# Revit family: Catena UL LED - Folded
name_source: partatom
category: Lighting Fixtures
units: mm (PartAtom-declared; Revit-internal decimal feet)

## family parameters
Always vertical = Yes
Cut with Voids When Loaded = No
Host = Wall
Light Source = Yes
OmniClass Number = 23.80.70.00
OmniClass Title = Lighting
Part Type = Normal
Room Calculation Point = No
Round Connector Dimension = Use Diameter
Shared = No

## types (2) — shared parameters
Color Filter = 16777215
Dimmable = No
Dimming Lamp Color Temperature Shift = <None>
Driver Included = Yes
Driver Required = No
Emit from Line Length = 610 mm
Main Finish = Polished Chrome
Manufacturer = Astro Lighting Ltd
Product Name = Catena LED
URL = www.astrolighting.com
zero-valued in all types: Default Elevation

## per-type parameters (varying)
| type | ADA compliant | Apparent Load | Dimming Method | Efficacy (lm/w) | Electrical Class | Lamp | Length of Cable Supplied | Light Source Fixed | Location rating | Main Material | Photometric Web File | Power (Watts) | Product Code | Product Location | Product SKU | Tilt Angle |
| CE |  | 32 VA |  | 21 | 2 | Dedicated LED |  | Yes | IP44 | Stainless Steel | GNC-1755 Catena LED.ies | 12.4 | 8592 | Zone 2, 3 | 1137003 | 60.00° |
| ETL | NO | 0 VA | Not Applicable | 32 | 1 | Integral LED | Not Applicable | Adjustable | DAMP | Metal - Zinc | 1137004_Catena LED_Photometry_IES_Iss.01.ies | 8.9 | 8647 | Bathroom | 1137004 | 90.00° |

## geometry (parser evidence)
native form markers: Sweep x3
no freeform markers — native parametric forms only
